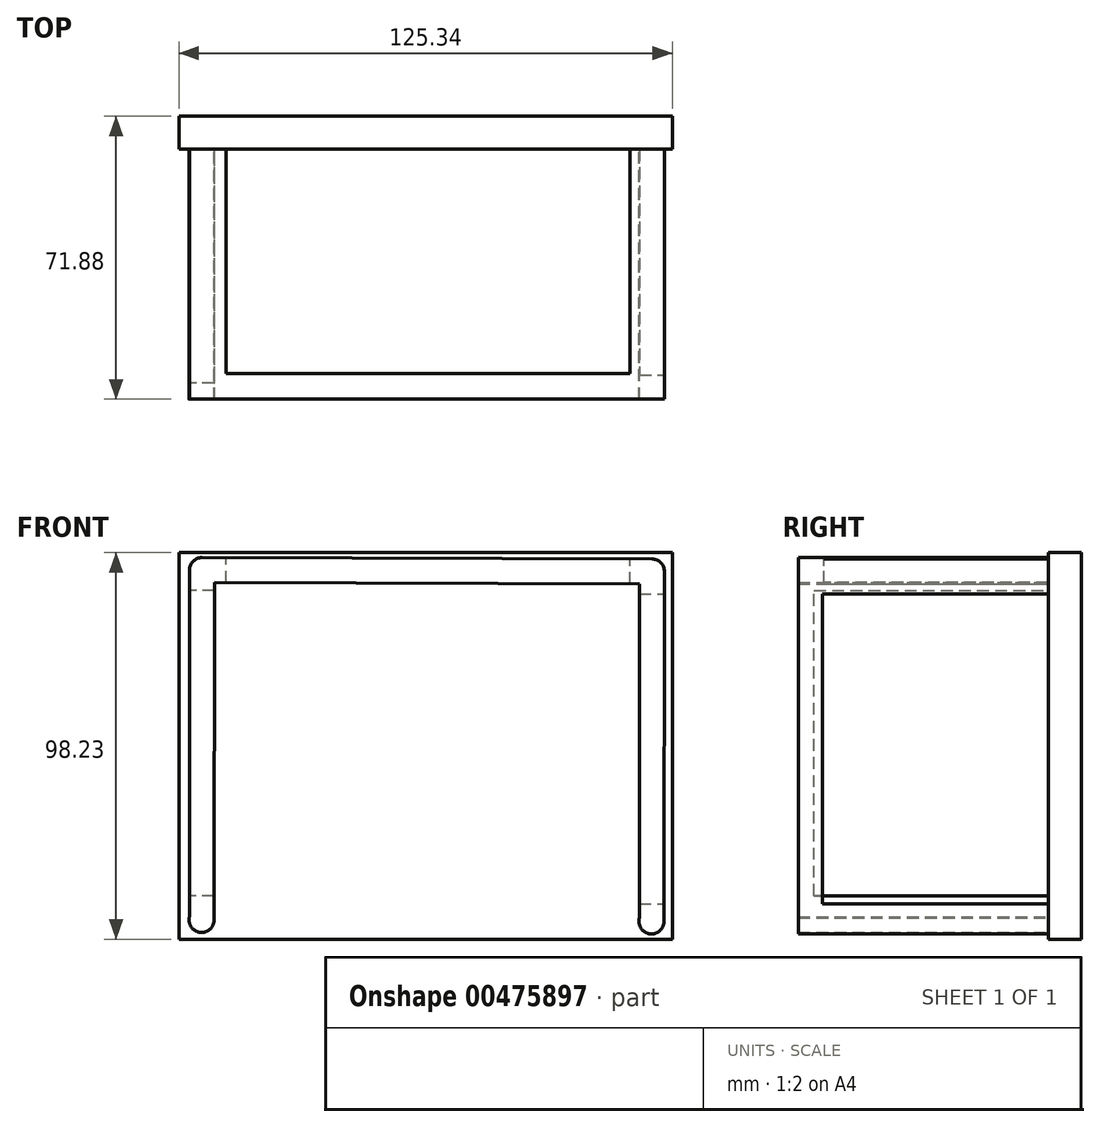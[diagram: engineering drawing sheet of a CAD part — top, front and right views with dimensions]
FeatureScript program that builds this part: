
annotation { "Feature Type Name" : "Feature", "Feature Type Description" : "" }
export const myFeature = defineFeature(function(context is Context, id is Id, definition is map)
    precondition{}
    {
        {
            var Q0;
            Q0=qCreatedBy(makeId("Front.planeOp"),FACE);
            var sketch = newSketch(context, id + "F0", { "sketchPlane" : qUnion([Q0])});
            skCircle(sketch, "E0", {"center": v(-62.35, 42.05) * mm, "radius": 3.18 * mm});
            skCircle(sketch, "E1", {"center": v(51.95, 41.68) * mm, "radius": 3.18 * mm});
            skCircle(sketch, "E2", {"center": v(-62.47, -46.85) * mm, "radius": 3.18 * mm});
            skCircle(sketch, "E3", {"center": v(51.83, -47.22) * mm, "radius": 3.18 * mm});
            skLineSegment(sketch, "E4", {"start": v(-59.18, 42.05) * mm, "end": v(-59.3, -46.85) * mm});
            skLineSegment(sketch, "E5", {"start": v(-62.35, 38.88) * mm, "end": v(51.94, 38.5) * mm});
            skLineSegment(sketch, "E6", {"start": v(-62.35, 45.23) * mm, "end": v(51.96, 44.86) * mm});
            skLineSegment(sketch, "E7", {"start": v(48.77, 41.68) * mm, "end": v(48.77, -47.22) * mm});
            skLineSegment(sketch, "E8", {"start": v(55, -47.22) * mm, "end": v(55.12, 41.68) * mm});
            skLineSegment(sketch, "E9", {"start": v(-59.18, 42.05) * mm, "end": v(-68.7, 42.06) * mm, "construction": true});
            skLineSegment(sketch, "E10", {"start": v(-65.53, 42.06) * mm, "end": v(-65.53, -47.7) * mm});
            skSolve(sketch);
        }
        {
            var Q0;
            Q0 = qSketchRegion(id + "F0", true);
            extrude(context, id + "F1", {"entities" : qUnion([Q0]), "depth" : 63.5 * mm});
        }
        {
            var Q0;
            Q0=makeQuery(id+"F1.opExtrude","SWEPT_FACE",FACE,{"disambiguationData":[OSD([sQuery(id+"F0.wireOp",EDGE,"E10")])]});
            var sketch = newSketch(context, id + "F2", { "sketchPlane" : qUnion([Q0])});
            skLineSegment(sketch, "E11", {"start": v(0, 36.87) * mm, "end": v(59.46, 36.87) * mm});
            skLineSegment(sketch, "E12", {"start": v(59.46, 36.87) * mm, "end": v(59.46, -40.66) * mm});
            skLineSegment(sketch, "E13", {"start": v(59.46, -40.66) * mm, "end": v(0, -40.66) * mm});
            skSolve(sketch);
        }
        {
            var Q0;
            {var subQ0=sQuery(id+"F2.wireOp",EDGE,"E11");Q0=makeQuery(id+"F2.imprint","IMPRINT",FACE,{"disambiguationData":[TD([[makeQuery(id+"F2.imprint","IMPRINT",EDGE,{"derivedFrom":subQ0}),-1.0]])]});}
            extrude(context, id + "F3", {"entities" : qUnion([Q0]), "operationType" : NewBodyOperationType.REMOVE, "oppositeDirection" : true, "depth" : 25.4 * mm});
        }
        {
            var Q0;
            Q0=makeQuery(id+"F1.opExtrude","SWEPT_FACE",FACE,{"disambiguationData":[OSD([sQuery(id+"F0.wireOp",EDGE,"E6")])]});
            var sketch = newSketch(context, id + "F4", { "sketchPlane" : qUnion([Q0])});
            skLineSegment(sketch, "E14", {"start": v(-56.4, 0) * mm, "end": v(-56.4, -56.98) * mm});
            skLineSegment(sketch, "E15", {"start": v(-56.4, -56.98) * mm, "end": v(46.2, -56.98) * mm});
            skLineSegment(sketch, "E16", {"start": v(46.2, -56.98) * mm, "end": v(46.2, 0) * mm});
            skSolve(sketch);
        }
        {
            var Q0;
            {var subQ0=sQuery(id+"F4.wireOp",EDGE,"E14");Q0=makeQuery(id+"F4.imprint","IMPRINT",FACE,{"disambiguationData":[TD([[makeQuery(id+"F4.imprint","IMPRINT",EDGE,{"derivedFrom":subQ0}),1.0]])]});}
            extrude(context, id + "F5", {"entities" : qUnion([Q0]), "operationType" : NewBodyOperationType.REMOVE, "oppositeDirection" : true, "depth" : 25.4 * mm});
        }
        {
            var Q0;
            Q0=makeQuery(id+"F1.opExtrude","SWEPT_FACE",FACE,{"disambiguationData":[OSD([sQuery(id+"F0.wireOp",EDGE,"E8")])]});
            var sketch = newSketch(context, id + "F6", { "sketchPlane" : qUnion([Q0])});
            skLineSegment(sketch, "E17", {"start": v(0, 36.07) * mm, "end": v(-57.42, 36.07) * mm});
            skLineSegment(sketch, "E18", {"start": v(-57.42, 36.07) * mm, "end": v(-57.42, -42.63) * mm});
            skLineSegment(sketch, "E19", {"start": v(-57.42, -42.63) * mm, "end": v(0, -42.63) * mm});
            skSolve(sketch);
        }
        {
            var Q0;
            {var subQ0=sQuery(id+"F6.wireOp",EDGE,"E17");Q0=makeQuery(id+"F6.imprint","IMPRINT",FACE,{"disambiguationData":[TD([[makeQuery(id+"F6.imprint","IMPRINT",EDGE,{"derivedFrom":subQ0}),1.0]])]});}
            extrude(context, id + "F7", {"entities" : qUnion([Q0]), "operationType" : NewBodyOperationType.REMOVE, "oppositeDirection" : true, "depth" : 25.4 * mm});
        }
        {
            var Q0;
            Q0=qCreatedBy(makeId("Front.planeOp"),FACE);
            var sketch = newSketch(context, id + "F8", { "sketchPlane" : qUnion([Q0])});
            skLineSegment(sketch, "E20.bottom", {"start": v(57.13, 46.5) * mm, "end": v(-68.2, 46.5) * mm});
            skLineSegment(sketch, "E20.top", {"start": v(57.13, -51.74) * mm, "end": v(-68.2, -51.74) * mm});
            skLineSegment(sketch, "E20.left", {"start": v(57.13, 46.5) * mm, "end": v(57.13, -51.74) * mm});
            skLineSegment(sketch, "E20.right", {"start": v(-68.2, 46.5) * mm, "end": v(-68.2, -51.74) * mm});
            skSolve(sketch);
        }
        {
            var Q0;
            Q0 = qSketchRegion(id + "F8", true);
            extrude(context, id + "F9", {"entities" : qUnion([Q0]), "operationType" : NewBodyOperationType.ADD, "oppositeDirection" : true, "depth" : 8.38 * mm});
        }
    });
